FCSTD DOCUMENT  (FreeCAD 0.18.4R)
Label: salleDeBain
License: All rights reserved
LicenseURL: http://en.wikipedia.org/wiki/All_rights_reserved
objects: Sketcher::SketchObject×1, PartDesign::Body×1
note: 2 computed .brp shape members not serialized (recipe doc carries the construction recipe); baked Part::Feature solids carry a one-line shape summary decoded from their .brp

FEATURE [Sketcher::SketchObject] Sketch
  MapMode = 5
  Support = -> [XY_Plane]
  sketch-geometry (8):
    g0: LineSegment StartX=0 StartY=0 StartZ=0 EndX=0 EndY=2890 EndZ=0
    g1: LineSegment StartX=1600 StartY=2945.87 StartZ=0 EndX=0 EndY=2890 EndZ=0
    g2: LineSegment StartX=0 StartY=0 StartZ=0 EndX=820 EndY=0 EndZ=0
    g3: LineSegment StartX=1600 StartY=727.362 StartZ=0 EndX=1600 EndY=2945.87 EndZ=0
    g4: LineSegment StartX=820 StartY=0 StartZ=0 EndX=1600 EndY=727.362 EndZ=0
    g5: LineSegment StartX=2250 StartY=2968.57 StartZ=0 EndX=2250 EndY=727.362 EndZ=0
    g6: LineSegment StartX=1600 StartY=2945.87 StartZ=0 EndX=2250 EndY=2968.57 EndZ=0
    g7: LineSegment StartX=1600 StartY=727.362 StartZ=0 EndX=2250 EndY=727.362 EndZ=0
  constraints (22):
    c: Vertical(g0)
    c: Coincident(g0,g-1)
    c: Distance(g0) = 2890
    c: Coincident(g1,g0)
    c: Angle(g0,g1) = 1.6057
    c: Horizontal(g2)
    c: Distance(g2) = 820
    c: Coincident(g2,g0)
    c: Vertical(g3)
    c: DistanceX(g0,g3) = 1600
    c: Angle(g4,g2) = 2.3911
    c: Coincident(g2,g4)
    c: Coincident(g3,g4)
    c: Coincident(g1,g3)
    c: Vertical(g5)
    c: DistanceX(g1,g5) = 650
    c: Coincident(g6,g1)
    c: Coincident(g6,g5)
    c: Parallel(g1,g6)
    c: Horizontal(g3,g5)
    c: Coincident(g7,g3)
    c: Coincident(g7,g5)
FEATURE [PartDesign::Body] Body
  Group = -> [Sketch]
  Origin = -> Origin
